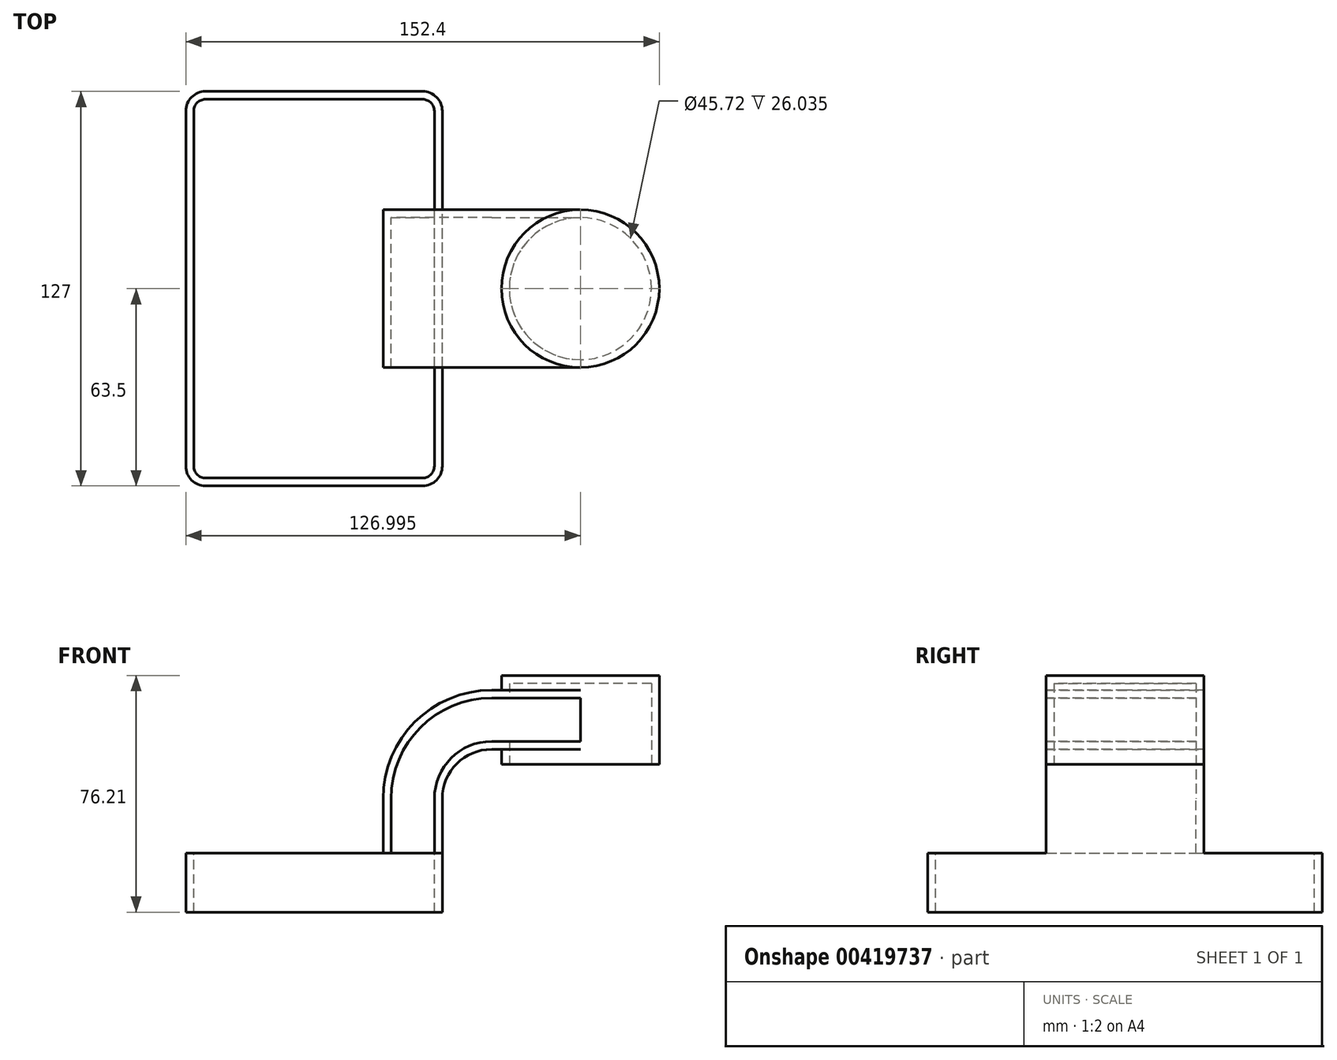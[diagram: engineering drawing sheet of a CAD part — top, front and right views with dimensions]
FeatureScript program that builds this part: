
annotation { "Feature Type Name" : "Feature", "Feature Type Description" : "" }
export const myFeature = defineFeature(function(context is Context, id is Id, definition is map)
    precondition{}
    {
        {
            var Q0;
            Q0=qCreatedBy(makeId("Front.planeOp"),FACE);
            var sketch = newSketch(context, id + "F0", { "sketchPlane" : qUnion([Q0])});
            skLineSegment(sketch, "E0.bottom", {"start": v(-41.28, -9.53) * mm, "end": v(41.28, -9.53) * mm});
            skLineSegment(sketch, "E0.top", {"start": v(-41.28, 9.53) * mm, "end": v(41.28, 9.53) * mm});
            skLineSegment(sketch, "E0.left", {"start": v(-41.28, -9.53) * mm, "end": v(-41.28, 9.53) * mm});
            skLineSegment(sketch, "E0.right", {"start": v(41.28, -9.53) * mm, "end": v(41.28, 9.52) * mm});
            skPoint(sketch, "E0.middle", {"position": v(0, 0) * mm});
            skLineSegment(sketch, "E1.bottom", {"start": v(111.12, 38.1) * mm, "end": v(60.33, 38.1) * mm});
            skLineSegment(sketch, "E1.top", {"start": v(111.12, 66.68) * mm, "end": v(60.33, 66.68) * mm});
            skLineSegment(sketch, "E1.left", {"start": v(111.12, 38.1) * mm, "end": v(111.12, 66.68) * mm});
            skLineSegment(sketch, "E1.right", {"start": v(60.33, 38.1) * mm, "end": v(60.33, 66.68) * mm});
            skPoint(sketch, "E1.middle", {"position": v(85.72, 52.39) * mm});
            skLineSegment(sketch, "E2", {"start": v(41.27, 9.52) * mm, "end": v(41.27, 27) * mm});
            skArc(sketch, "E3", {"start": v(41.27, 27) * mm, "mid": v(45.92, 38.23) * mm, "end": v(57.15, 42.88) * mm});
            skLineSegment(sketch, "E4", {"start": v(57.15, 42.88) * mm, "end": v(85.72, 42.88) * mm});
            skLineSegment(sketch, "E5.0", {"start": v(57.15, 61.93) * mm, "end": v(85.72, 61.93) * mm});
            skArc(sketch, "E5.1", {"start": v(22.23, 27) * mm, "mid": v(32.45, 51.7) * mm, "end": v(57.15, 61.93) * mm});
            skLineSegment(sketch, "E5.2", {"start": v(22.22, 9.52) * mm, "end": v(22.22, 27) * mm});
            skLineSegment(sketch, "E6", {"start": v(85.72, 42.88) * mm, "end": v(85.72, 61.93) * mm});
            skLineSegment(sketch, "E7", {"start": v(85.72, 61.93) * mm, "end": v(85.72, 66.68) * mm});
            skPoint(sketch, "E7.endSnap0", {"position": v(85.72, 66.68) * mm});
            skFitSpline(sketch, "E8", {"points": [v(-41.28, 9.53) * mm, v(57.15, 61.93) * mm], "startDerivative": vector(1.42, 85.45) * mm, "endDerivative": vector(117.98, -0.7) * mm});
            skLineSegment(sketch, "E9", {"start": v(85.72, 42.88) * mm, "end": v(85.72, 38.1) * mm});
            skSolve(sketch);
        }
        {
            var Q0;
            Q0=makeQuery(id+"F0.imprint","IMPRINT",FACE,{"disambiguationData":[TD([[makeQuery(id+"F0.imprint","IMPRINT",EDGE,{"derivedFrom":sQuery(id+"F0.wireOp",EDGE,"E0.bottom")}),1.0]])]});
            extrude(context, id + "F1", {"entities" : qUnion([Q0]), "endBound" : BoundingType.SYMMETRIC, "depth" : 127 * mm});
        }
        {
            var Q0;
            {var subQ1=sQuery(id+"F0.wireOp",EDGE,"E2");Q0=makeQuery(id+"F0.imprint","IMPRINT",FACE,{"disambiguationData":[TD([[makeQuery(id+"F0.imprint","IMPRINT",EDGE,{"derivedFrom":subQ1}),1.0]])]});}
            var Q1;
            {var subQ5=sQuery(id+"F0.wireOp",EDGE,"E6");Q1=makeQuery(id+"F0.imprint","IMPRINT",FACE,{"disambiguationData":[TD([[makeQuery(id+"F0.imprint","IMPRINT",EDGE,{"derivedFrom":subQ5}),1.0]])]});}
            extrude(context, id + "F2", {"entities" : qUnion([Q0, Q1]), "operationType" : NewBodyOperationType.ADD, "endBound" : BoundingType.SYMMETRIC, "depth" : 50.8 * mm});
        }
        {
            var Q0;
            Q0=makeQuery(id+"F0.imprint","IMPRINT",FACE,{"disambiguationData":[TD([[makeQuery(id+"F0.imprint","IMPRINT",EDGE,{"derivedFrom":sQuery(id+"F0.wireOp",EDGE,"E5.1")}),1.0]])]});
            extrude(context, id + "F3", {"entities" : qUnion([Q0]), "operationType" : NewBodyOperationType.ADD, "endBound" : BoundingType.SYMMETRIC, "depth" : 15.88 * mm});
        }
        {
            var Q0;
            {var subQ0=sQuery(id+"F0.wireOp",EDGE,"E1.left");Q0=makeQuery(id+"F0.imprint","IMPRINT",FACE,{"disambiguationData":[TD([[makeQuery(id+"F0.imprint","IMPRINT",EDGE,{"derivedFrom":subQ0}),1.0]])]});}
            var Q1;
            Q1=sQuery(id+"F0.wireOp",EDGE,"E6");
            revolve(context, id + "F4", {"operationType" : NewBodyOperationType.ADD, "entities" : qUnion([Q0]), "axis" : qUnion([Q1]), "revolveType" : RevolveType.FULL});
        }
        {
            var Q0;
            Q0=makeQuery(id+"F1.opExtrude","CAP_EDGE",EDGE,{"disambiguationData":[OSD([sQuery(id+"F0.wireOp",EDGE,"E0.right")])],"isStart":false});
            var Q1;
            Q1=makeQuery(id+"F1.opExtrude","CAP_EDGE",EDGE,{"disambiguationData":[OSD([sQuery(id+"F0.wireOp",EDGE,"E0.left")])],"isStart":false});
            var Q2;
            Q2=makeQuery(id+"F1.opExtrude","CAP_EDGE",EDGE,{"disambiguationData":[OSD([sQuery(id+"F0.wireOp",EDGE,"E0.right")])],"isStart":true});
            var Q3;
            Q3=makeQuery(id+"F1.opExtrude","CAP_EDGE",EDGE,{"disambiguationData":[OSD([sQuery(id+"F0.wireOp",EDGE,"E0.left")])],"isStart":true});
            fillet(context, id + "F5", {"entities" : qUnion([Q0, Q1, Q2, Q3]), "radius" : 6.35 * mm, "tangentPropagation" : true, "allowEdgeOverflow" : false});
        }
        {
            var Q0;
            Q0=makeQuery(id+"F1.opExtrude","SWEPT_FACE",FACE,{"disambiguationData":[OSD([sQuery(id+"F0.wireOp",EDGE,"E0.bottom")])]});
            var Q1;
            Q1=makeQuery(id+"F4.opRevolve","SWEPT_FACE",FACE,{"disambiguationData":[OSD([sQuery(id+"F0.wireOp",EDGE,"E1.bottom")])]});
            var Q2;
            Q2=makeQuery(id+"F2.opExtrude","CAP_FACE",FACE,{"disambiguationData":[OSD([sQuery(id+"F0.wireOp",EDGE,"E0.top"),sQuery(id+"F0.wireOp",EDGE,"E2"),sQuery(id+"F0.wireOp",EDGE,"E3"),sQuery(id+"F0.wireOp",EDGE,"E4"),sQuery(id+"F0.wireOp",EDGE,"E5.0"),sQuery(id+"F0.wireOp",EDGE,"E5.1"),sQuery(id+"F0.wireOp",EDGE,"E5.2"),sQuery(id+"F0.wireOp",EDGE,"E6")])],"isStart":false});
            var Q3;
            Q3=makeQuery(id+"F3.opExtrude","CAP_FACE",FACE,{"disambiguationData":[OSD([sQuery(id+"F0.wireOp",EDGE,"E0.top"),sQuery(id+"F0.wireOp",EDGE,"E5.1"),sQuery(id+"F0.wireOp",EDGE,"E5.2"),sQuery(id+"F0.wireOp",EDGE,"E8")])],"isStart":false});
            var Q4;
            {var subQ3=sQuery(id+"F0.wireOp",EDGE,"E0.top");var subQ4=sQuery(id+"F0.wireOp",EDGE,"E0.right");var subQ5=sQuery(id+"F0.wireOp",EDGE,"E0.left");Q4=makeQuery(id+"F3.boolean.opBoolean","SPLIT",FACE,{"disambiguationData":[TD([makeQuery(id+"F1.opExtrude","CAP_FACE",FACE,{"disambiguationData":[OSD([sQuery(id+"F0.wireOp",EDGE,"E0.bottom"),subQ3,subQ5,subQ4])],"isStart":true})])],"derivedFrom":makeQuery(id+"F1.opExtrude","SWEPT_FACE",FACE,{"disambiguationData":[OSD([subQ3])]})});}
            var Q5;
            {var subQ3=sQuery(id+"F0.wireOp",EDGE,"E0.top");var subQ5=sQuery(id+"F0.wireOp",EDGE,"E0.right");var subQ6=sQuery(id+"F0.wireOp",EDGE,"E0.left");Q5=makeQuery(id+"F3.boolean.opBoolean","SPLIT",FACE,{"disambiguationData":[TD([makeQuery(id+"F1.opExtrude","CAP_FACE",FACE,{"disambiguationData":[OSD([sQuery(id+"F0.wireOp",EDGE,"E0.bottom"),subQ3,subQ6,subQ5])],"isStart":false})])],"derivedFrom":makeQuery(id+"F1.opExtrude","SWEPT_FACE",FACE,{"disambiguationData":[OSD([subQ3])]})});}
            var Q6;
            Q6=makeQuery(id+"F3.opExtrude","CAP_FACE",FACE,{"disambiguationData":[OSD([sQuery(id+"F0.wireOp",EDGE,"E0.top"),sQuery(id+"F0.wireOp",EDGE,"E5.1"),sQuery(id+"F0.wireOp",EDGE,"E5.2"),sQuery(id+"F0.wireOp",EDGE,"E8")])],"isStart":true});
            shell(context, id + "F6", {"entities" : qUnion([Q0, Q1, Q2, Q3, Q4, Q5, Q6]), "thickness" : 2.54 * mm});
        }
    });
